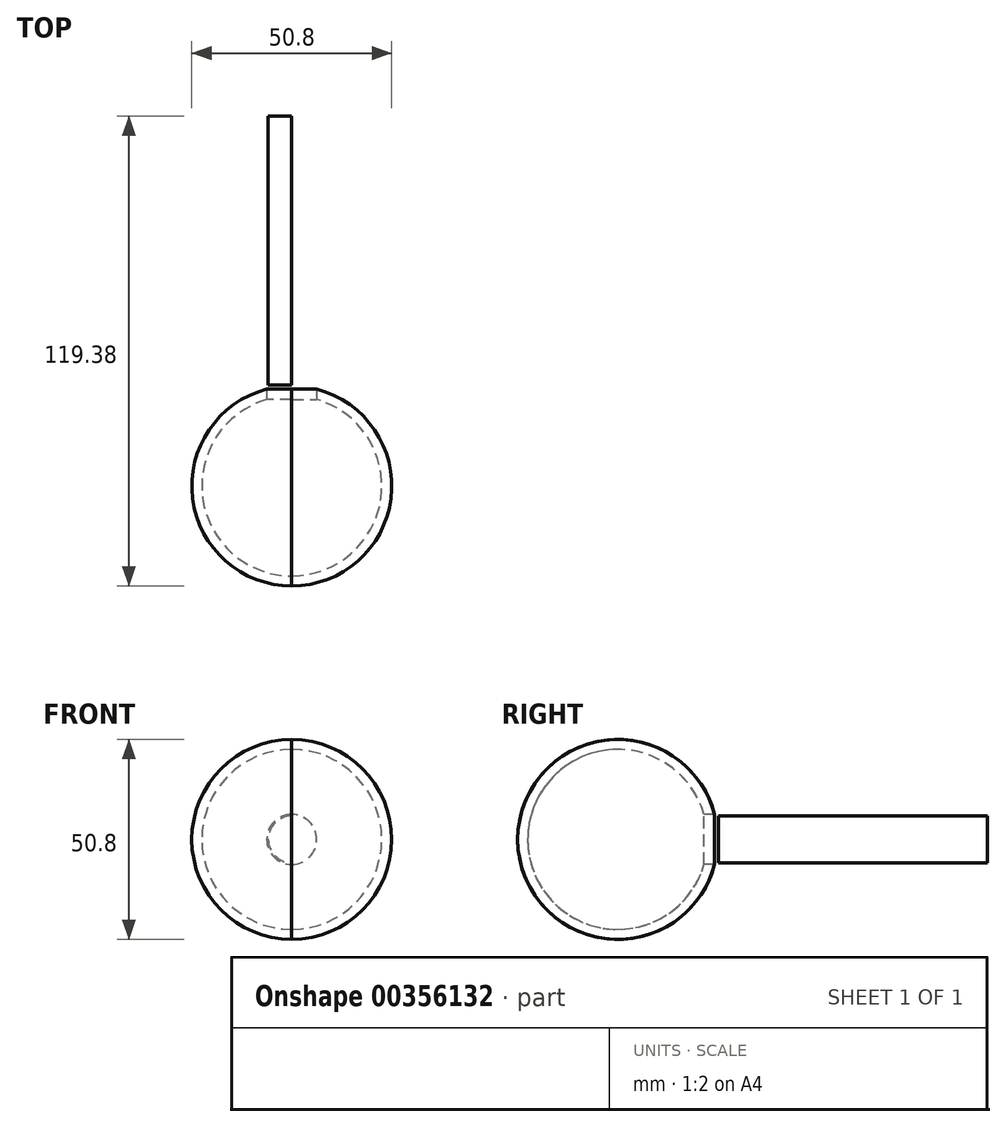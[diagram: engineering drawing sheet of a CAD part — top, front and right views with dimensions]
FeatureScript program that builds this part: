
annotation { "Feature Type Name" : "Feature", "Feature Type Description" : "" }
export const myFeature = defineFeature(function(context is Context, id is Id, definition is map)
    precondition{}
    {
        {
            var Q0;
            Q0=qCreatedBy(makeId("Front.planeOp"),FACE);
            var sketch = newSketch(context, id + "F0", { "sketchPlane" : qUnion([Q0])});
            skLineSegment(sketch, "E0", {"start": v(0, -25.4) * mm, "end": v(0, -25.4) * mm});
            skLineSegment(sketch, "E1", {"start": v(0, 25.4) * mm, "end": v(0, 25.4) * mm});
            skArc(sketch, "E2", {"start": v(0, 25.4) * mm, "mid": v(-17.11, 18.77) * mm, "end": v(-25.3, 2.34) * mm});
            skArc(sketch, "E3", {"start": v(0, -25.4) * mm, "mid": v(18.8, -17.07) * mm, "end": v(25.28, 2.45) * mm});
            skLineSegment(sketch, "E4", {"start": v(0, -25.4) * mm, "end": v(0, 25.4) * mm});
            skArc(sketch, "E5", {"start": v(-25.3, 2.34) * mm, "mid": v(-18.77, -17.11) * mm, "end": v(0, -25.4) * mm});
            skArc(sketch, "E6", {"start": v(25.28, 2.45) * mm, "mid": v(17.07, 18.8) * mm, "end": v(0, 25.4) * mm});
            skSolve(sketch);
        }
        {
            var Q0;
            Q0=makeQuery(id+"F0.imprint","IMPRINT",FACE,{"disambiguationData":[TD([[makeQuery(id+"F0.imprint","IMPRINT",EDGE,{"derivedFrom":sQuery(id+"F0.wireOp",EDGE,"E3")}),1.0]])]});
            var Q1;
            Q1=sQuery(id+"F0.wireOp",EDGE,"E4");
            revolve(context, id + "F1", {"entities" : qUnion([Q0]), "axis" : qUnion([Q1]), "revolveType" : RevolveType.TWO_DIRECTIONS, "angle" : 270 * degree, "angleBack" : 90 * degree});
        }
        {
            var Q0;
            Q0=qCreatedBy(makeId("Front.planeOp"),FACE);
            var sketch = newSketch(context, id + "F2", { "sketchPlane" : qUnion([Q0])});
            skLineSegment(sketch, "E7", {"start": v(0, 22.86) * mm, "end": v(0, -22.86) * mm});
            skArc(sketch, "E8", {"start": v(0, 22.86) * mm, "mid": v(-22.86, 0) * mm, "end": v(0, -22.86) * mm});
            skArc(sketch, "E9", {"start": v(0, -22.86) * mm, "mid": v(22.86, 0) * mm, "end": v(0, 22.86) * mm});
            skSolve(sketch);
        }
        {
            var Q0;
            Q0=makeQuery(id+"F2.imprint","IMPRINT",FACE,{"disambiguationData":[TD([[makeQuery(id+"F2.imprint","IMPRINT",EDGE,{"derivedFrom":sQuery(id+"F2.wireOp",EDGE,"E7")}),-1.0]])]});
            var Q1;
            Q1=sQuery(id+"F2.wireOp",EDGE,"E7");
            revolve(context, id + "F3", {"operationType" : NewBodyOperationType.REMOVE, "entities" : qUnion([Q0]), "axis" : qUnion([Q1]), "revolveType" : RevolveType.FULL, "oppositeDirection" : true});
        }
        {
            var Q0;
            Q0=qCreatedBy(makeId("Front.planeOp"),FACE);
            var sketch = newSketch(context, id + "F4", { "sketchPlane" : qUnion([Q0])});
            skLineSegment(sketch, "E10", {"start": v(0, -5.97) * mm, "end": v(0, 5.97) * mm});
            skArc(sketch, "E11", {"start": v(0, -5.97) * mm, "mid": v(5.97, 0) * mm, "end": v(0, 5.97) * mm});
            skArc(sketch, "E12", {"start": v(0, 5.97) * mm, "mid": v(-5.97, 0) * mm, "end": v(0, -5.97) * mm});
            skSolve(sketch);
        }
        {
            var Q0;
            Q0=makeQuery(id+"F4.imprint","IMPRINT",FACE,{"disambiguationData":[TD([[makeQuery(id+"F4.imprint","IMPRINT",EDGE,{"derivedFrom":sQuery(id+"F4.wireOp",EDGE,"E10")}),1.0]])]});
            extrude(context, id + "F5", {"entities" : qUnion([Q0]), "oppositeDirection" : true, "depth" : 93.98 * mm, "hasSecondDirection" : true, "secondDirectionOppositeDirection" : true, "secondDirectionDepth" : 25.4 * mm});
        }
        {
            var Q0;
            Q0=qCreatedBy(makeId("Right.planeOp"),FACE);
            var sketch = newSketch(context, id + "F6", { "sketchPlane" : qUnion([Q0])});
            skLineSegment(sketch, "E13", {"start": v(22.86, 0) * mm, "end": v(-22.86, 0) * mm});
            skArc(sketch, "E14", {"start": v(22.86, 0) * mm, "mid": v(0, 22.86) * mm, "end": v(-22.86, 0) * mm});
            skArc(sketch, "E15", {"start": v(-22.86, 0) * mm, "mid": v(0, -22.86) * mm, "end": v(22.86, 0) * mm});
            skLineSegment(sketch, "E16", {"start": v(25.4, 0) * mm, "end": v(-25.4, 0) * mm});
            skArc(sketch, "E17", {"start": v(25.4, 0) * mm, "mid": v(0, 25.4) * mm, "end": v(-25.4, 0) * mm});
            skArc(sketch, "E18", {"start": v(-25.4, 0) * mm, "mid": v(0, -25.4) * mm, "end": v(25.4, 0) * mm});
            skSolve(sketch);
        }
        {
            var Q0;
            {var subQ0=sQuery(id+"F6.wireOp",EDGE,"E14");Q0=makeQuery(id+"F6.imprint","IMPRINT",FACE,{"disambiguationData":[TD([[makeQuery(id+"F6.imprint","IMPRINT",EDGE,{"derivedFrom":subQ0}),-1.0]])]});}
            var Q1;
            Q1=sQuery(id+"F6.wireOp",EDGE,"E16");
            revolve(context, id + "F7", {"entities" : qUnion([Q0]), "axis" : qUnion([Q1]), "revolveType" : RevolveType.TWO_DIRECTIONS, "angle" : 0 * degree, "angleBack" : 180 * degree});
        }
        {
            var Q0;
            Q0=qCreatedBy(makeId("Front.planeOp"),FACE);
            var sketch = newSketch(context, id + "F8", { "sketchPlane" : qUnion([Q0])});
            skCircle(sketch, "E19", {"center": v(0, 0) * mm, "radius": 6.35 * mm});
            skSolve(sketch);
        }
        {
            var Q0;
            Q0 = qSketchRegion(id + "F8", true);
            extrude(context, id + "F9", {"entities" : qUnion([Q0]), "operationType" : NewBodyOperationType.REMOVE, "oppositeDirection" : true, "depth" : 25.65 * mm});
        }
        {
            var Q0;
            Q0 = qSketchRegion(id + "F8", true);
            extrude(context, id + "F10", {"entities" : qUnion([Q0]), "operationType" : NewBodyOperationType.REMOVE, "oppositeDirection" : true, "depth" : 24.9 * mm});
        }
    });
